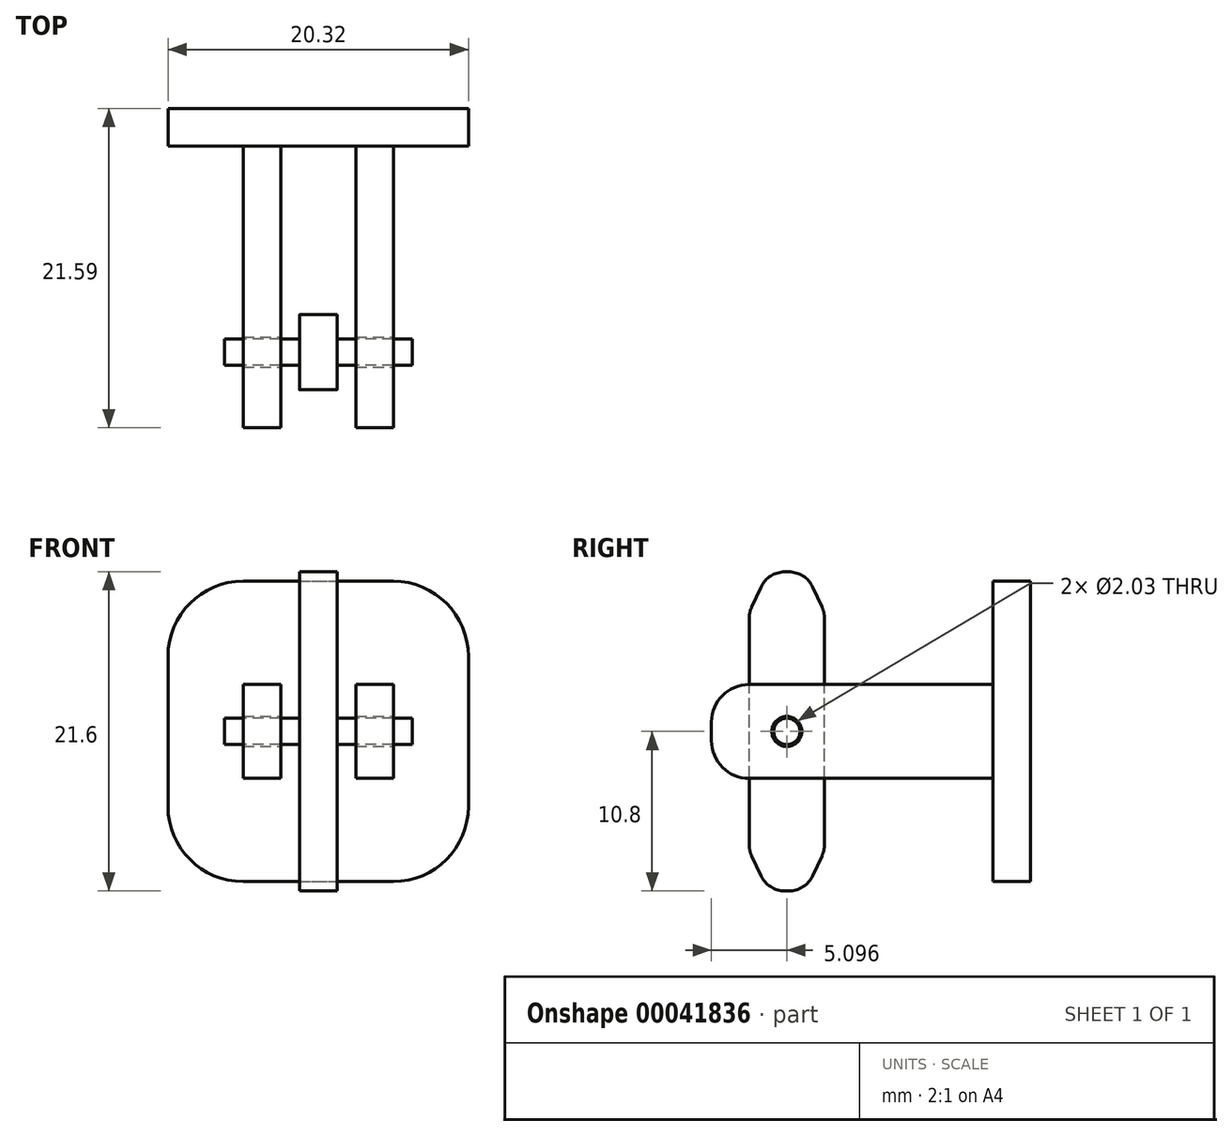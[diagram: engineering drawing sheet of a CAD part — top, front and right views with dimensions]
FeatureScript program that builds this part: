
annotation { "Feature Type Name" : "Feature", "Feature Type Description" : "" }
export const myFeature = defineFeature(function(context is Context, id is Id, definition is map)
    precondition{}
    {
        {
            var Q0;
            Q0=qCreatedBy(makeId("Front.planeOp"),FACE);
            var sketch = newSketch(context, id + "F0", { "sketchPlane" : qUnion([Q0])});
            skLineSegment(sketch, "E0.bottom", {"start": v(-10.16, 10.16) * mm, "end": v(10.16, 10.16) * mm});
            skLineSegment(sketch, "E0.top", {"start": v(-10.16, -10.16) * mm, "end": v(10.16, -10.16) * mm});
            skLineSegment(sketch, "E0.left", {"start": v(-10.16, 10.16) * mm, "end": v(-10.16, -10.16) * mm});
            skLineSegment(sketch, "E0.right", {"start": v(10.16, 10.16) * mm, "end": v(10.16, -10.16) * mm});
            skLineSegment(sketch, "E1", {"start": v(0, 0) * mm, "end": v(0, 20.68) * mm, "construction": true});
            skSolve(sketch);
        }
        {
            var Q0;
            Q0 = qSketchRegion(id + "F0", true);
            extrude(context, id + "F1", {"entities" : qUnion([Q0]), "depth" : 2.54 * mm});
        }
        {
            var Q0;
            Q0=makeQuery(id+"F1.opExtrude","CAP_FACE",FACE,{"disambiguationData":[OSD([sQuery(id+"F0.wireOp",EDGE,"E0.bottom"),sQuery(id+"F0.wireOp",EDGE,"E0.top"),sQuery(id+"F0.wireOp",EDGE,"E0.left"),sQuery(id+"F0.wireOp",EDGE,"E0.right")])],"isStart":false});
            var sketch = newSketch(context, id + "F2", { "sketchPlane" : qUnion([Q0])});
            skLineSegment(sketch, "E2.bottom", {"start": v(-5.08, 3.17) * mm, "end": v(-2.54, 3.17) * mm});
            skLineSegment(sketch, "E2.top", {"start": v(-5.08, -3.18) * mm, "end": v(-2.54, -3.18) * mm});
            skLineSegment(sketch, "E2.left", {"start": v(-5.08, 3.18) * mm, "end": v(-5.08, -3.18) * mm});
            skLineSegment(sketch, "E2.right", {"start": v(-2.54, 3.18) * mm, "end": v(-2.54, -3.18) * mm});
            skLineSegment(sketch, "E3", {"start": v(0, 0) * mm, "end": v(0, 6.83) * mm, "construction": true});
            skLineSegment(sketch, "E4.MirrorCS", {"start": v(2.54, 3.18) * mm, "end": v(2.54, -3.18) * mm});
            skLineSegment(sketch, "E5.MirrorCS", {"start": v(5.08, 3.18) * mm, "end": v(5.08, -3.18) * mm});
            skLineSegment(sketch, "E6.MirrorCS", {"start": v(5.08, -3.18) * mm, "end": v(2.54, -3.18) * mm});
            skLineSegment(sketch, "E7.MirrorCS", {"start": v(5.08, 3.17) * mm, "end": v(2.54, 3.17) * mm});
            skLineSegment(sketch, "E8", {"start": v(0, 0) * mm, "end": v(-28.13, 0) * mm, "construction": true});
            skSolve(sketch);
        }
        {
            var Q0;
            Q0=makeQuery(id+"F2.imprint","IMPRINT",FACE,{"disambiguationData":[TD([[makeQuery(id+"F2.imprint","IMPRINT",EDGE,{"derivedFrom":sQuery(id+"F2.wireOp",EDGE,"E2.bottom")}),-1.0]])]});
            var Q1;
            Q1=makeQuery(id+"F2.imprint","IMPRINT",FACE,{"disambiguationData":[TD([[makeQuery(id+"F2.imprint","IMPRINT",EDGE,{"derivedFrom":sQuery(id+"F2.wireOp",EDGE,"E4.MirrorCS")}),1.0]])]});
            extrude(context, id + "F3", {"entities" : qUnion([Q0, Q1]), "operationType" : NewBodyOperationType.ADD, "depth" : 19.05 * mm});
        }
        {
            var Q0;
            Q0=makeQuery(id+"F3.boolean.opBoolean","MERGE",FACE,{"derivedFrom":[makeQuery(id+"F1.opExtrude","SWEPT_FACE",FACE,{"disambiguationData":[OSD([sQuery(id+"F0.wireOp",EDGE,"E0.right")])]}),makeQuery(id+"F3.opExtrude","SWEPT_FACE",FACE,{"disambiguationData":[OSD([sQuery(id+"F2.wireOp",EDGE,"E5.MirrorCS")])]})]});
            var sketch = newSketch(context, id + "F4", { "sketchPlane" : qUnion([Q0])});
            skCircle(sketch, "E9", {"center": v(-16.5, 0) * mm, "radius": 1.02 * mm});
            skLineSegment(sketch, "E10", {"start": v(-21.59, 0) * mm, "end": v(-2.06, 0) * mm, "construction": true});
            skSolve(sketch);
        }
        {
            var Q0;
            Q0 = qSketchRegion(id + "F4", true);
            extrude(context, id + "F5", {"entities" : qUnion([Q0]), "operationType" : NewBodyOperationType.REMOVE, "endBound" : BoundingType.THROUGH_ALL, "oppositeDirection" : true, "depth" : 25.4 * mm});
        }
        {
            var Q0;
            Q0=qCreatedBy(makeId("Right.planeOp"),FACE);
            var sketch = newSketch(context, id + "F6", { "sketchPlane" : qUnion([Q0])});
            skLineSegment(sketch, "E11.bottom", {"start": v(-19.03, -10.8) * mm, "end": v(-13.95, -10.8) * mm});
            skLineSegment(sketch, "E11.top", {"start": v(-19.03, 10.8) * mm, "end": v(-13.95, 10.8) * mm});
            skLineSegment(sketch, "E11.left", {"start": v(-19.03, -10.8) * mm, "end": v(-19.03, 10.8) * mm});
            skLineSegment(sketch, "E11.right", {"start": v(-13.95, -10.8) * mm, "end": v(-13.95, 10.8) * mm});
            skLineSegment(sketch, "E12", {"start": v(-16.5, 0) * mm, "end": v(-16.5, -6.69) * mm, "construction": true});
            skLineSegment(sketch, "E13", {"start": v(-16.5, 0) * mm, "end": v(4.44, 0) * mm, "construction": true});
            skSolve(sketch);
        }
        {
            var Q0;
            Q0=makeQuery(id+"F6.imprint","IMPRINT",FACE,{"disambiguationData":[TD([[makeQuery(id+"F6.imprint","IMPRINT",EDGE,{"derivedFrom":sQuery(id+"F6.wireOp",EDGE,"E11.bottom")}),1.0]])]});
            extrude(context, id + "F7", {"entities" : qUnion([Q0]), "operationType" : NewBodyOperationType.ADD, "endBound" : BoundingType.SYMMETRIC, "depth" : 2.54 * mm});
        }
        {
            var Q0;
            Q0=qCreatedBy(makeId("Right.planeOp"),FACE);
            var sketch = newSketch(context, id + "F8", { "sketchPlane" : qUnion([Q0])});
            skCircle(sketch, "E14", {"center": v(-16.5, 0) * mm, "radius": 0.89 * mm});
            skSolve(sketch);
        }
        {
            var Q0;
            Q0 = qSketchRegion(id + "F8", true);
            extrude(context, id + "F9", {"entities" : qUnion([Q0]), "operationType" : NewBodyOperationType.ADD, "endBound" : BoundingType.SYMMETRIC, "depth" : 12.7 * mm});
        }
        {
            var Q0;
            Q0=makeQuery(id+"F3.opExtrude","CAP_EDGE",EDGE,{"disambiguationData":[OSD([sQuery(id+"F2.wireOp",EDGE,"E7.MirrorCS")])],"isStart":false});
            var Q1;
            Q1=makeQuery(id+"F3.opExtrude","CAP_EDGE",EDGE,{"disambiguationData":[OSD([sQuery(id+"F2.wireOp",EDGE,"E2.bottom")])],"isStart":false});
            var Q2;
            Q2=makeQuery(id+"F3.opExtrude","CAP_EDGE",EDGE,{"disambiguationData":[OSD([sQuery(id+"F2.wireOp",EDGE,"E2.top")])],"isStart":false});
            var Q3;
            Q3=makeQuery(id+"F3.opExtrude","CAP_EDGE",EDGE,{"disambiguationData":[OSD([sQuery(id+"F2.wireOp",EDGE,"E6.MirrorCS")])],"isStart":false});
            fillet(context, id + "F10", {"entities" : qUnion([Q0, Q1, Q2, Q3]), "radius" : 2.54 * mm, "tangentPropagation" : true, "allowEdgeOverflow" : false});
        }
        {
            var Q0;
            Q0=makeQuery(id+"F7.opExtrude","SWEPT_EDGE",EDGE,{"disambiguationData":[OSD([sQuery(id+"F6.wireOp",EDGE,"E11.top"),sQuery(id+"F6.wireOp",EDGE,"E11.right")])]});
            var Q1;
            Q1=makeQuery(id+"F7.opExtrude","SWEPT_EDGE",EDGE,{"disambiguationData":[OSD([sQuery(id+"F6.wireOp",EDGE,"E11.top"),sQuery(id+"F6.wireOp",EDGE,"E11.left")])]});
            var Q2;
            Q2=makeQuery(id+"F7.opExtrude","SWEPT_EDGE",EDGE,{"disambiguationData":[OSD([sQuery(id+"F6.wireOp",EDGE,"E11.bottom"),sQuery(id+"F6.wireOp",EDGE,"E11.left")])]});
            var Q3;
            Q3=makeQuery(id+"F7.opExtrude","SWEPT_EDGE",EDGE,{"disambiguationData":[OSD([sQuery(id+"F6.wireOp",EDGE,"E11.bottom"),sQuery(id+"F6.wireOp",EDGE,"E11.right")])]});
            chamfer(context, id + "F11", {"entities" : qUnion([Q0, Q1, Q2, Q3]), "chamferType" : ChamferType.OFFSET_ANGLE, "width" : 1.27 * mm, "oppositeDirection" : false, "angle" : 65 * degree, "tangentPropagation" : true});
        }
        {
            var Q0;
            {var subQ0=sQuery(id+"F6.wireOp",EDGE,"E11.right");Q0=makeQuery(id+"F11.opChamfer","BLEND_EDGE",EDGE,{"blendedFrom":[makeQuery(id+"F7.opExtrude","SWEPT_EDGE",EDGE,{"disambiguationData":[OSD([sQuery(id+"F6.wireOp",EDGE,"E11.top"),subQ0])]}),makeQuery(id+"F7.opExtrude","SWEPT_FACE",FACE,{"disambiguationData":[OSD([subQ0])]})],"blendedInto":[makeQuery(id+"F7.opExtrude","SWEPT_FACE",FACE,{"disambiguationData":[OSD([subQ0])]})]});}
            var Q1;
            {var subQ0=sQuery(id+"F6.wireOp",EDGE,"E11.top");Q1=makeQuery(id+"F11.opChamfer","BLEND_EDGE",EDGE,{"blendedFrom":[makeQuery(id+"F7.opExtrude","SWEPT_EDGE",EDGE,{"disambiguationData":[OSD([subQ0,sQuery(id+"F6.wireOp",EDGE,"E11.right")])]}),makeQuery(id+"F7.opExtrude","SWEPT_FACE",FACE,{"disambiguationData":[OSD([subQ0])]})],"blendedInto":[makeQuery(id+"F7.opExtrude","SWEPT_FACE",FACE,{"disambiguationData":[OSD([subQ0])]})]});}
            var Q2;
            {var subQ0=sQuery(id+"F6.wireOp",EDGE,"E11.top");Q2=makeQuery(id+"F11.opChamfer","BLEND_EDGE",EDGE,{"blendedFrom":[makeQuery(id+"F7.opExtrude","SWEPT_EDGE",EDGE,{"disambiguationData":[OSD([subQ0,sQuery(id+"F6.wireOp",EDGE,"E11.left")])]}),makeQuery(id+"F7.opExtrude","SWEPT_FACE",FACE,{"disambiguationData":[OSD([subQ0])]})],"blendedInto":[makeQuery(id+"F7.opExtrude","SWEPT_FACE",FACE,{"disambiguationData":[OSD([subQ0])]})]});}
            var Q3;
            {var subQ0=sQuery(id+"F6.wireOp",EDGE,"E11.left");Q3=makeQuery(id+"F11.opChamfer","BLEND_EDGE",EDGE,{"blendedFrom":[makeQuery(id+"F7.opExtrude","SWEPT_EDGE",EDGE,{"disambiguationData":[OSD([sQuery(id+"F6.wireOp",EDGE,"E11.top"),subQ0])]}),makeQuery(id+"F7.opExtrude","SWEPT_FACE",FACE,{"disambiguationData":[OSD([subQ0])]})],"blendedInto":[makeQuery(id+"F7.opExtrude","SWEPT_FACE",FACE,{"disambiguationData":[OSD([subQ0])]})]});}
            var Q4;
            {var subQ0=sQuery(id+"F6.wireOp",EDGE,"E11.right");Q4=makeQuery(id+"F11.opChamfer","BLEND_EDGE",EDGE,{"blendedFrom":[makeQuery(id+"F7.opExtrude","SWEPT_EDGE",EDGE,{"disambiguationData":[OSD([sQuery(id+"F6.wireOp",EDGE,"E11.bottom"),subQ0])]}),makeQuery(id+"F7.opExtrude","SWEPT_FACE",FACE,{"disambiguationData":[OSD([subQ0])]})],"blendedInto":[makeQuery(id+"F7.opExtrude","SWEPT_FACE",FACE,{"disambiguationData":[OSD([subQ0])]})]});}
            var Q5;
            {var subQ0=sQuery(id+"F6.wireOp",EDGE,"E11.bottom");Q5=makeQuery(id+"F11.opChamfer","BLEND_EDGE",EDGE,{"blendedFrom":[makeQuery(id+"F7.opExtrude","SWEPT_EDGE",EDGE,{"disambiguationData":[OSD([subQ0,sQuery(id+"F6.wireOp",EDGE,"E11.right")])]}),makeQuery(id+"F7.opExtrude","SWEPT_FACE",FACE,{"disambiguationData":[OSD([subQ0])]})],"blendedInto":[makeQuery(id+"F7.opExtrude","SWEPT_FACE",FACE,{"disambiguationData":[OSD([subQ0])]})]});}
            var Q6;
            {var subQ0=sQuery(id+"F6.wireOp",EDGE,"E11.bottom");Q6=makeQuery(id+"F11.opChamfer","BLEND_EDGE",EDGE,{"blendedFrom":[makeQuery(id+"F7.opExtrude","SWEPT_EDGE",EDGE,{"disambiguationData":[OSD([subQ0,sQuery(id+"F6.wireOp",EDGE,"E11.left")])]}),makeQuery(id+"F7.opExtrude","SWEPT_FACE",FACE,{"disambiguationData":[OSD([subQ0])]})],"blendedInto":[makeQuery(id+"F7.opExtrude","SWEPT_FACE",FACE,{"disambiguationData":[OSD([subQ0])]})]});}
            var Q7;
            {var subQ0=sQuery(id+"F6.wireOp",EDGE,"E11.left");Q7=makeQuery(id+"F11.opChamfer","BLEND_EDGE",EDGE,{"blendedFrom":[makeQuery(id+"F7.opExtrude","SWEPT_EDGE",EDGE,{"disambiguationData":[OSD([sQuery(id+"F6.wireOp",EDGE,"E11.bottom"),subQ0])]}),makeQuery(id+"F7.opExtrude","SWEPT_FACE",FACE,{"disambiguationData":[OSD([subQ0])]})],"blendedInto":[makeQuery(id+"F7.opExtrude","SWEPT_FACE",FACE,{"disambiguationData":[OSD([subQ0])]})]});}
            fillet(context, id + "F12", {"entities" : qUnion([Q0, Q1, Q2, Q3, Q4, Q5, Q6, Q7]), "radius" : 1.78 * mm, "tangentPropagation" : true, "allowEdgeOverflow" : false});
        }
        {
            var Q0;
            Q0=makeQuery(id+"F1.opExtrude","SWEPT_EDGE",EDGE,{"disambiguationData":[OSD([sQuery(id+"F0.wireOp",EDGE,"E0.bottom"),sQuery(id+"F0.wireOp",EDGE,"E0.right")])]});
            var Q1;
            Q1=makeQuery(id+"F1.opExtrude","SWEPT_EDGE",EDGE,{"disambiguationData":[OSD([sQuery(id+"F0.wireOp",EDGE,"E0.bottom"),sQuery(id+"F0.wireOp",EDGE,"E0.left")])]});
            var Q2;
            Q2=makeQuery(id+"F1.opExtrude","SWEPT_EDGE",EDGE,{"disambiguationData":[OSD([sQuery(id+"F0.wireOp",EDGE,"E0.top"),sQuery(id+"F0.wireOp",EDGE,"E0.right")])]});
            var Q3;
            Q3=makeQuery(id+"F1.opExtrude","SWEPT_EDGE",EDGE,{"disambiguationData":[OSD([sQuery(id+"F0.wireOp",EDGE,"E0.top"),sQuery(id+"F0.wireOp",EDGE,"E0.left")])]});
            fillet(context, id + "F13", {"entities" : qUnion([Q0, Q1, Q2, Q3]), "radius" : 5.08 * mm, "tangentPropagation" : true, "allowEdgeOverflow" : false});
        }
    });
